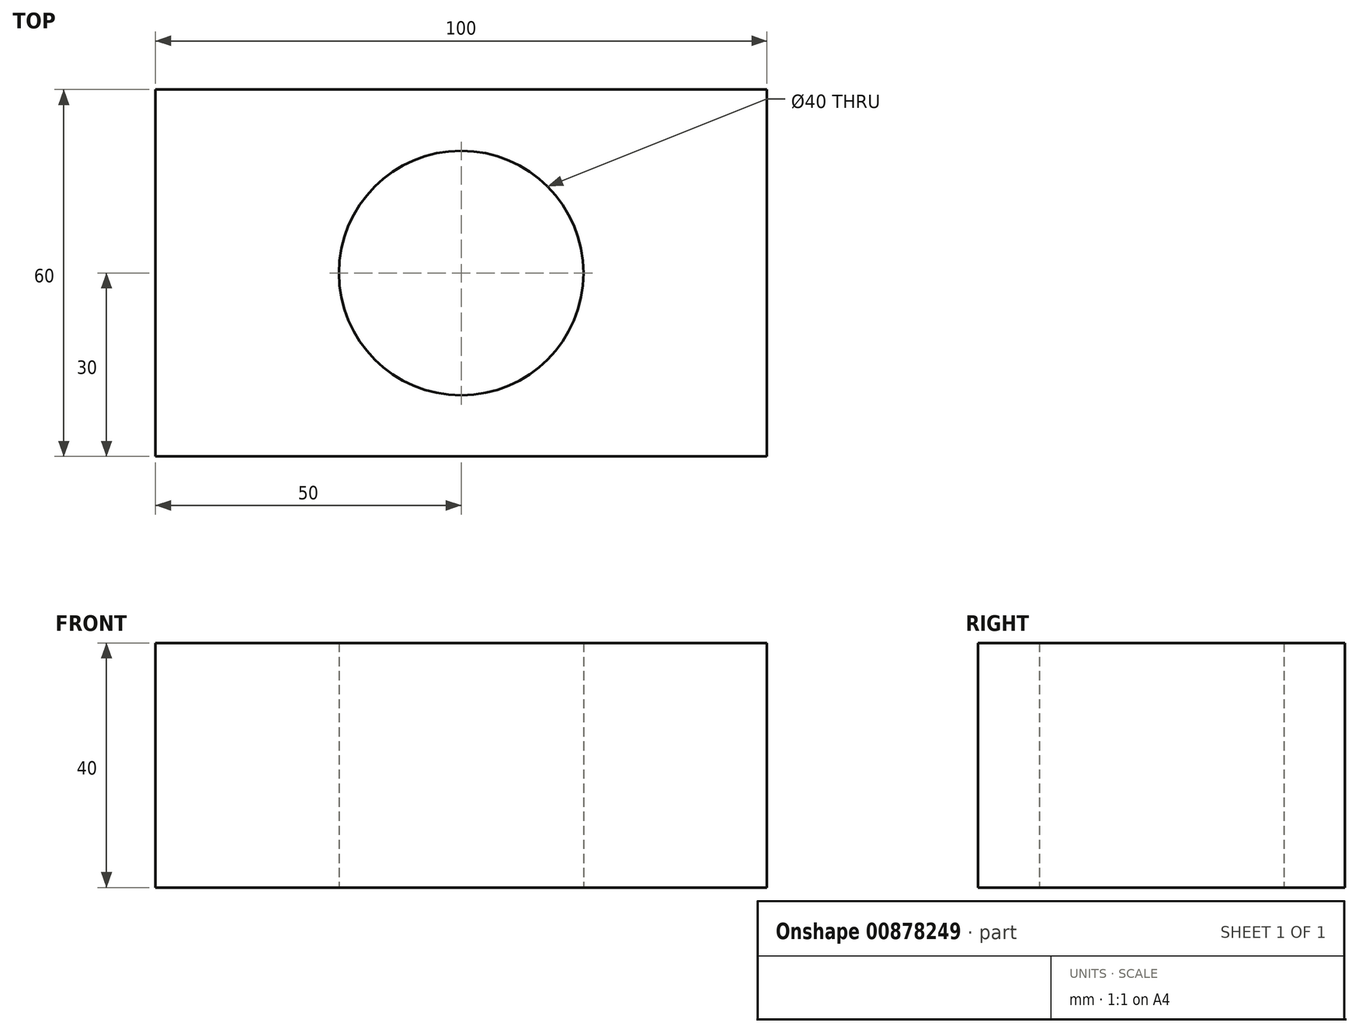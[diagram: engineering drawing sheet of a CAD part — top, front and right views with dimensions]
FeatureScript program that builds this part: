
annotation { "Feature Type Name" : "Feature", "Feature Type Description" : "" }
export const myFeature = defineFeature(function(context is Context, id is Id, definition is map)
    precondition{}
    {
        {
            var Q0;
            Q0=qCreatedBy(makeId("Top.planeOp"),FACE);
            var sketch = newSketch(context, id + "F0", { "sketchPlane" : qUnion([Q0])});
            skLineSegment(sketch, "E0.bottom", {"start": v(0, 60) * mm, "end": v(100, 60) * mm});
            skLineSegment(sketch, "E0.top", {"start": v(0, 0) * mm, "end": v(100, 0) * mm});
            skLineSegment(sketch, "E0.left", {"start": v(0, 60) * mm, "end": v(0, 0) * mm});
            skLineSegment(sketch, "E0.right", {"start": v(100, 60) * mm, "end": v(100, 0) * mm});
            skCircle(sketch, "E1", {"center": v(50, 30) * mm, "radius": 20 * mm});
            skLineSegment(sketch, "E2", {"start": v(0, 60) * mm, "end": v(100, 0) * mm, "construction": true});
            skSolve(sketch);
        }
        {
            var Q0;
            Q0=makeQuery(id+"F0.imprint","IMPRINT",FACE,{"disambiguationData":[TD([[makeQuery(id+"F0.imprint","IMPRINT",EDGE,{"derivedFrom":sQuery(id+"F0.wireOp",EDGE,"E0.bottom")}),-1.0]])]});
            extrude(context, id + "F1", {"entities" : qUnion([Q0]), "depth" : 40 * mm, "offsetDistance" : 25.4 * mm});
        }
    });
